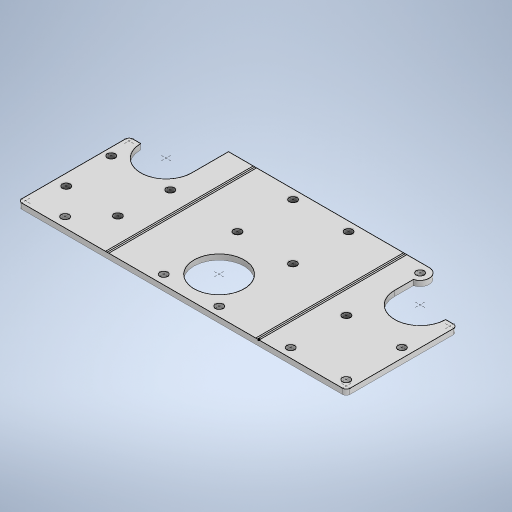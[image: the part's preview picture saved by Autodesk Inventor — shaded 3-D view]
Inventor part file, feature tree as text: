
AUTODESK INVENTOR PART (.ipt)
format: ipt  version: 2024.2 (Build 282272000, 272)  size: 297,472 bytes
history: native  units: in
note: dims shown in document units (in); Inventor stores cm internally (conversion verified against a paired STEP export)
features: sketch x1
ambient origin geometry x8: Origin, YZ Plane, XZ Plane, XY Plane, X Axis, Y Axis, Z Axis, Center Point
bodies: Body1 (feature_tree)
feature tree (1):
  sketch  "Sketch1"  dims[d3=0.0591in d4=0.0in]
